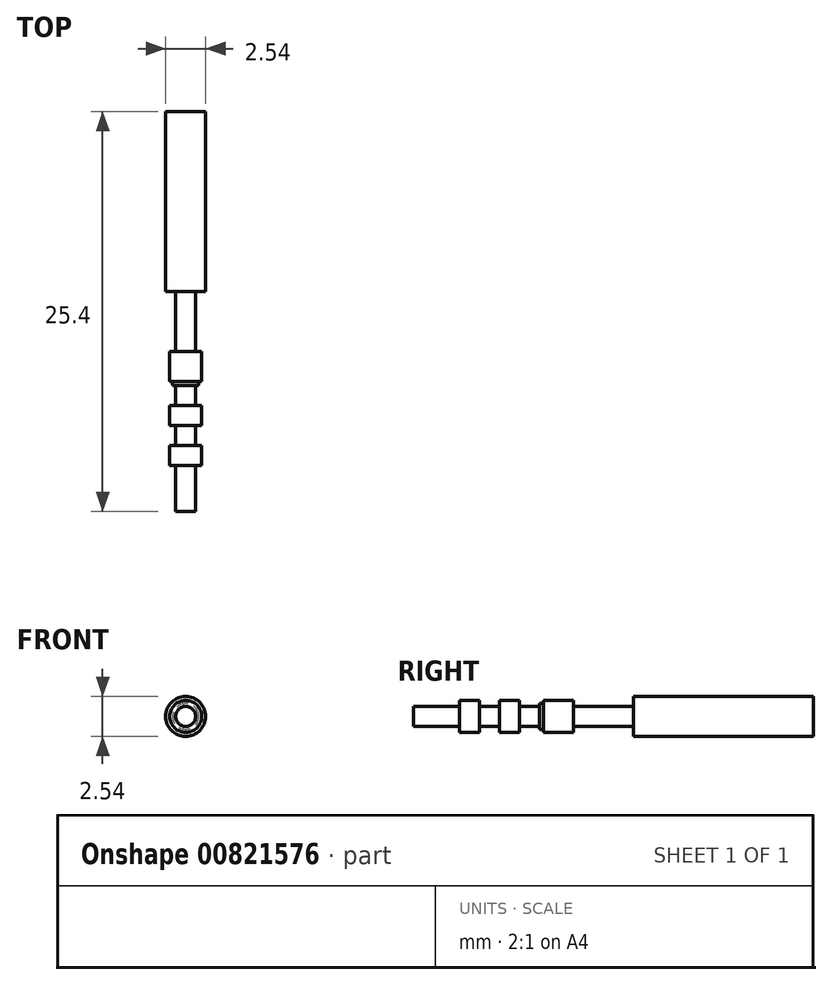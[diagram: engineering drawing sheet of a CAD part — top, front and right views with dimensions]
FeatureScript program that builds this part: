
annotation { "Feature Type Name" : "Feature", "Feature Type Description" : "" }
export const myFeature = defineFeature(function(context is Context, id is Id, definition is map)
    precondition{}
    {
        {
            var Q0;
            Q0=qCreatedBy(makeId("Right.planeOp"),FACE);
            var sketch = newSketch(context, id + "F0", { "sketchPlane" : qUnion([Q0])});
            skLineSegment(sketch, "E0", {"start": v(-50.5, 0) * mm, "end": v(49.98, 0) * mm, "construction": true});
            skLineSegment(sketch, "E1", {"start": v(0, 0) * mm, "end": v(0, 10.62) * mm, "construction": true});
            skLineSegment(sketch, "E2", {"start": v(0, 0) * mm, "end": v(-12.7, 0) * mm});
            skLineSegment(sketch, "E3.MirrorCS", {"start": v(0, 0) * mm, "end": v(12.7, 0) * mm});
            skLineSegment(sketch, "E4", {"start": v(-12.7, 0) * mm, "end": v(-12.7, 0.63) * mm});
            skLineSegment(sketch, "E5", {"start": v(-12.7, 0.63) * mm, "end": v(-9.78, 0.63) * mm});
            skLineSegment(sketch, "E6", {"start": v(-4.44, 0.83) * mm, "end": v(-4.44, 1.02) * mm});
            skLineSegment(sketch, "E7", {"start": v(-4.44, 1.02) * mm, "end": v(-2.54, 1.02) * mm});
            skLineSegment(sketch, "E8", {"start": v(-2.54, 1.02) * mm, "end": v(-2.54, 0.63) * mm});
            skLineSegment(sketch, "E9", {"start": v(-2.54, 0.64) * mm, "end": v(1.27, 0.64) * mm});
            skLineSegment(sketch, "E10", {"start": v(1.27, 0.63) * mm, "end": v(1.27, 1.27) * mm});
            skLineSegment(sketch, "E11", {"start": v(1.27, 1.27) * mm, "end": v(12.7, 1.27) * mm});
            skLineSegment(sketch, "E12", {"start": v(12.7, 1.27) * mm, "end": v(12.7, 0) * mm});
            skLineSegment(sketch, "E13", {"start": v(-4.44, 0.83) * mm, "end": v(-4.7, 0.83) * mm});
            skLineSegment(sketch, "E14", {"start": v(-4.7, 0.83) * mm, "end": v(-4.7, 0.63) * mm});
            skLineSegment(sketch, "E15", {"start": v(-5.97, 0.63) * mm, "end": v(-5.97, 1.02) * mm});
            skLineSegment(sketch, "E16", {"start": v(-5.97, 1.02) * mm, "end": v(-7.24, 1.02) * mm});
            skLineSegment(sketch, "E17", {"start": v(-7.24, 1.02) * mm, "end": v(-7.24, 0.63) * mm});
            skLineSegment(sketch, "E18", {"start": v(-8.5, 0.63) * mm, "end": v(-8.5, 1.02) * mm});
            skLineSegment(sketch, "E19", {"start": v(-8.5, 1.02) * mm, "end": v(-9.78, 1.02) * mm});
            skLineSegment(sketch, "E20", {"start": v(-9.78, 1.02) * mm, "end": v(-9.78, 0.63) * mm});
            skLineSegment(sketch, "E21.trimOffspring", {"start": v(-5.97, 0.63) * mm, "end": v(-4.7, 0.63) * mm});
            skLineSegment(sketch, "E22", {"start": v(-8.5, 0.63) * mm, "end": v(-7.24, 0.63) * mm});
            skSolve(sketch);
        }
        {
            var Q0;
            Q0 = qSketchRegion(id + "F0", true);
            var Q1;
            Q1=sQuery(id+"F0.wireOp",EDGE,"E2");
            revolve(context, id + "F1", {"surfaceOperationType" : NewSurfaceOperationType.NEW, "entities" : qUnion([Q0]), "axis" : qUnion([Q1]), "revolveType" : RevolveType.FULL});
        }
    });
